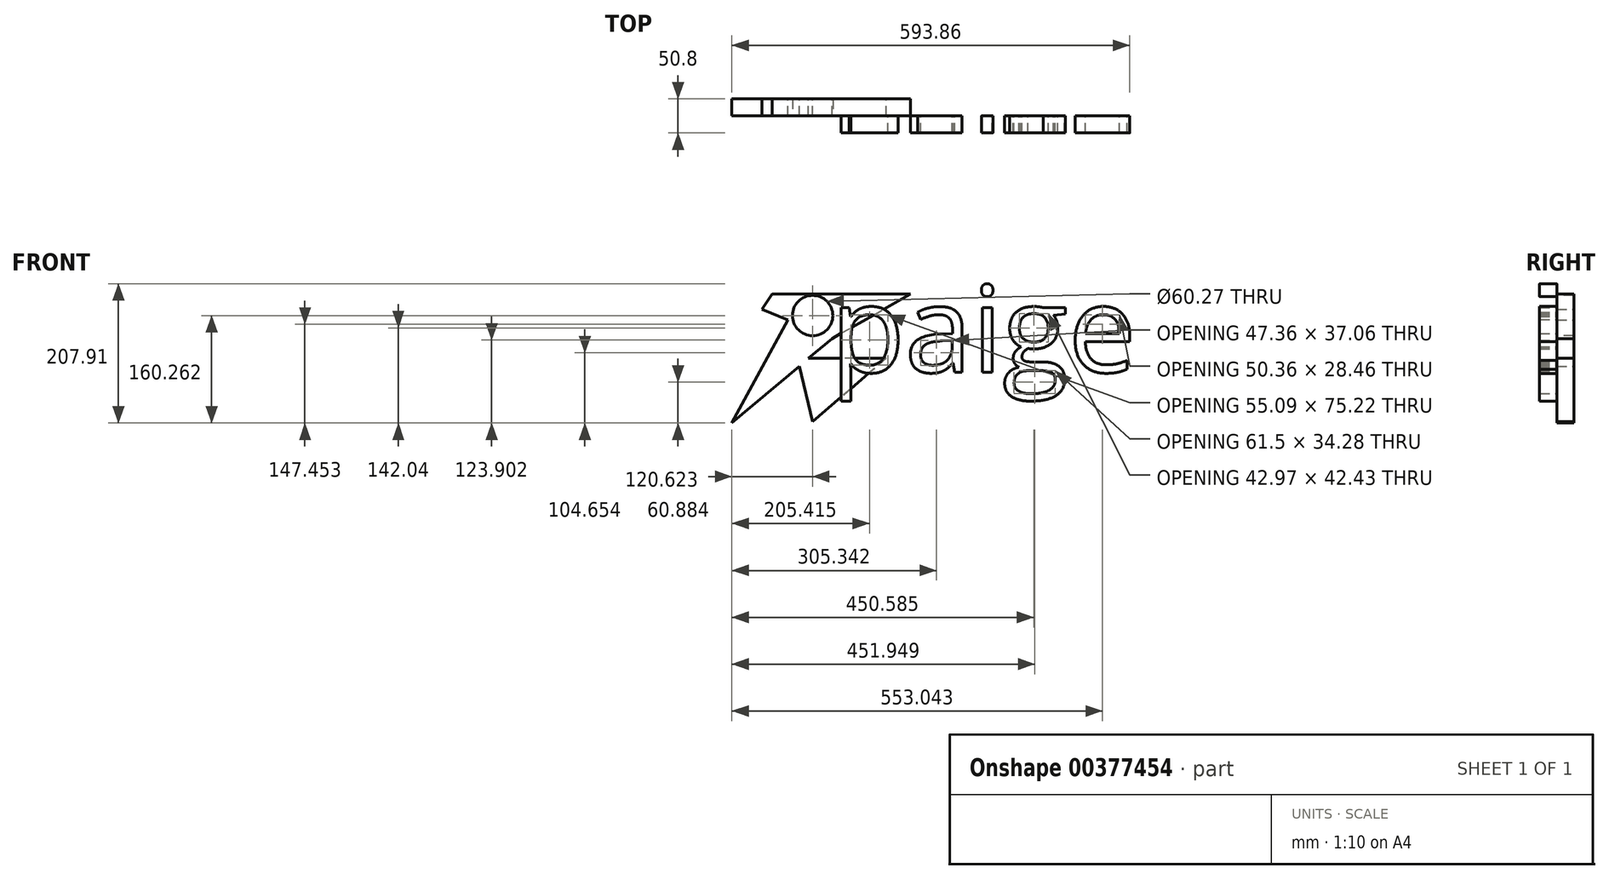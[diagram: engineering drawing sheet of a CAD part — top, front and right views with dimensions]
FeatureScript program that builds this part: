
annotation { "Feature Type Name" : "Feature", "Feature Type Description" : "" }
export const myFeature = defineFeature(function(context is Context, id is Id, definition is map)
    precondition{}
    {
        {
            var Q0;
            Q0=qCreatedBy(makeId("Front.planeOp"),FACE);
            var sketch = newSketch(context, id + "F0", { "sketchPlane" : qUnion([Q0])});
            skLineSegment(sketch, "E0", {"start": v(152.35, 22.9) * mm, "end": v(141.81, 129.33) * mm});
            skLineSegment(sketch, "E1", {"start": v(141.81, 129.33) * mm, "end": v(33.78, 106.53) * mm});
            skLineSegment(sketch, "E2", {"start": v(33.78, 106.53) * mm, "end": v(56.26, 0) * mm});
            skLineSegment(sketch, "E3", {"start": v(56.26, 0) * mm, "end": v(152.35, 22.9) * mm});
            skSolve(sketch);
        }
        {
            var Q0;
            Q0=qCreatedBy(makeId("Front.planeOp"),FACE);
            var sketch = newSketch(context, id + "F1", { "sketchPlane" : qUnion([Q0])});
            skLineSegment(sketch, "E4", {"start": v(23.13, -94.5) * mm, "end": v(0, 0) * mm});
            skLineSegment(sketch, "E5", {"start": v(0, 0) * mm, "end": v(168.75, 96.04) * mm});
            skLineSegment(sketch, "E6", {"start": v(168.75, 96.04) * mm, "end": v(-37.73, 96.04) * mm});
            skLineSegment(sketch, "E7", {"start": v(-37.73, 96.04) * mm, "end": v(-52.39, 73.29) * mm});
            skLineSegment(sketch, "E8", {"start": v(-52.39, 73.29) * mm, "end": v(51.78, 29.47) * mm});
            skLineSegment(sketch, "E9", {"start": v(51.78, 29.47) * mm, "end": v(-97.67, -96.46) * mm});
            skLineSegment(sketch, "E10", {"start": v(-97.67, -96.46) * mm, "end": v(-13.72, 57.02) * mm});
            skLineSegment(sketch, "E11", {"start": v(-13.72, 57.02) * mm, "end": v(0, 0) * mm});
            skLineSegment(sketch, "E12", {"start": v(132.83, 0) * mm, "end": v(0, 0) * mm});
            skLineSegment(sketch, "E13", {"start": v(132.83, 0) * mm, "end": v(23.13, -94.5) * mm});
            skLineSegment(sketch, "E14", {"start": v(161.3, 75.25) * mm, "end": v(168.75, 96.04) * mm});
            skLineSegment(sketch, "E15", {"start": v(152.84, 51.17) * mm, "end": v(161.3, 75.25) * mm});
            skSolve(sketch);
        }
        {
            var Q0;
            Q0 = qSketchRegion(id + "F1", true);
            extrude(context, id + "F2", {"entities" : qUnion([Q0]), "depth" : 25.4 * mm});
        }
        {
            var Q0;
            Q0=makeQuery(id+"F2.opExtrude","CAP_FACE",FACE,{"disambiguationData":[OSD([sQuery(id+"F1.wireOp",EDGE,"E4"),sQuery(id+"F1.wireOp",EDGE,"E5"),sQuery(id+"F1.wireOp",EDGE,"E6"),sQuery(id+"F1.wireOp",EDGE,"E7"),sQuery(id+"F1.wireOp",EDGE,"E8"),sQuery(id+"F1.wireOp",EDGE,"E9"),sQuery(id+"F1.wireOp",EDGE,"E10"),sQuery(id+"F1.wireOp",EDGE,"E12"),sQuery(id+"F1.wireOp",EDGE,"E13")])],"isStart":false});
            var sketch = newSketch(context, id + "F3", { "sketchPlane" : qUnion([Q0])});
            skCircle(sketch, "E16", {"center": v(22.95, 63.8) * mm, "radius": 30.14 * mm});
            skSolve(sketch);
        }
        {
            var Q0;
            Q0 = qSketchRegion(id + "F3", true);
            extrude(context, id + "F4", {"entities" : qUnion([Q0]), "operationType" : NewBodyOperationType.REMOVE, "oppositeDirection" : true, "depth" : 25.4 * mm});
        }
        {
            var Q0;
            Q0=makeQuery(id+"F2.opExtrude","CAP_FACE",FACE,{"disambiguationData":[OSD([sQuery(id+"F1.wireOp",EDGE,"E4"),sQuery(id+"F1.wireOp",EDGE,"E5"),sQuery(id+"F1.wireOp",EDGE,"E6"),sQuery(id+"F1.wireOp",EDGE,"E7"),sQuery(id+"F1.wireOp",EDGE,"E8"),sQuery(id+"F1.wireOp",EDGE,"E9"),sQuery(id+"F1.wireOp",EDGE,"E10"),sQuery(id+"F1.wireOp",EDGE,"E12"),sQuery(id+"F1.wireOp",EDGE,"E13")])],"isStart":false});
            var sketch = newSketch(context, id + "F5", { "sketchPlane" : qUnion([Q0])});
            skText(sketch, "E17", { "text": "paige", "fontName": "OpenSans-Regular.ttf"});
            const initialGuessF5  = {"E17": [0.05014, -0.02063, 1, 0, 0.12958]};
            skSetInitialGuess(sketch, initialGuessF5);
            skSolve(sketch);
        }
        {
            var Q0;
            Q0 = qSketchRegion(id + "F5", true);
            extrude(context, id + "F6", {"entities" : qUnion([Q0]), "depth" : 25.4 * mm});
        }
    });
